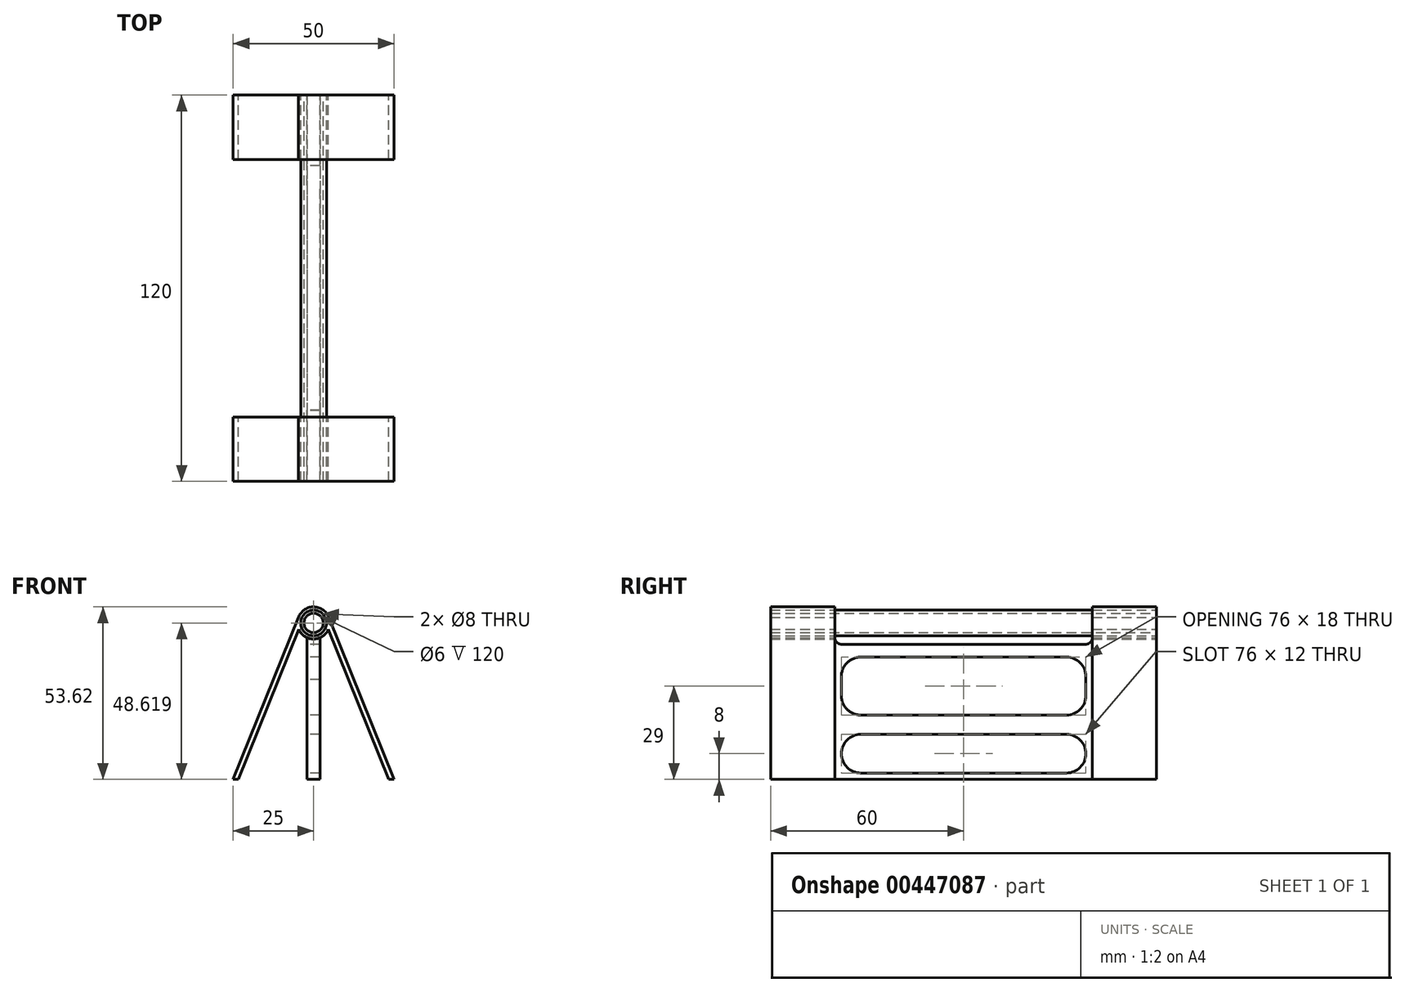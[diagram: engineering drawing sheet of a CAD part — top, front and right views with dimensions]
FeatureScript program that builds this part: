
annotation { "Feature Type Name" : "Feature", "Feature Type Description" : "" }
export const myFeature = defineFeature(function(context is Context, id is Id, definition is map)
    precondition{}
    {
        {
            var Q0;
            Q0=qCreatedBy(makeId("Right.planeOp"),FACE);
            var sketch = newSketch(context, id + "F0", { "sketchPlane" : qUnion([Q0])});
            skLineSegment(sketch, "E0.bottom", {"start": v(0, 48) * mm, "end": v(-120, 48) * mm});
            skLineSegment(sketch, "E0.top", {"start": v(0, 0) * mm, "end": v(-120, 0) * mm});
            skLineSegment(sketch, "E0.left", {"start": v(0, 48) * mm, "end": v(0, 0) * mm});
            skLineSegment(sketch, "E0.right", {"start": v(-120, 48) * mm, "end": v(-120, 0) * mm});
            skArc(sketch, "E1", {"start": v(-92, 32) * mm, "mid": v(-98, 26) * mm, "end": v(-92, 20) * mm});
            skArc(sketch, "E2", {"start": v(-28, 20) * mm, "mid": v(-22, 26) * mm, "end": v(-28, 32) * mm});
            skLineSegment(sketch, "E3", {"start": v(-92, 32) * mm, "end": v(-28, 32) * mm});
            skLineSegment(sketch, "E4", {"start": v(-28, 20) * mm, "end": v(-92, 20) * mm});
            skLineSegment(sketch, "E5", {"start": v(-92, 26) * mm, "end": v(-28, 26) * mm, "construction": true});
            skArc(sketch, "E6", {"start": v(-92, 14) * mm, "mid": v(-98, 8) * mm, "end": v(-92, 2) * mm});
            skArc(sketch, "E7", {"start": v(-28, 2) * mm, "mid": v(-22, 8) * mm, "end": v(-28, 14) * mm});
            skLineSegment(sketch, "E8", {"start": v(-92, 14) * mm, "end": v(-28, 14) * mm});
            skLineSegment(sketch, "E9", {"start": v(-28, 2) * mm, "end": v(-92, 2) * mm});
            skLineSegment(sketch, "E10", {"start": v(-92, 8) * mm, "end": v(-28, 8) * mm, "construction": true});
            skLineSegment(sketch, "E11", {"start": v(-60, 8) * mm, "end": v(-60, 26) * mm, "construction": true});
            skArc(sketch, "E12", {"start": v(-98, 46) * mm, "mid": v(-100, 44) * mm, "end": v(-98, 42) * mm});
            skArc(sketch, "E13", {"start": v(-22, 42) * mm, "mid": v(-20, 44) * mm, "end": v(-22, 46) * mm});
            skLineSegment(sketch, "E14", {"start": v(-98, 46) * mm, "end": v(-22, 46) * mm});
            skLineSegment(sketch, "E15", {"start": v(-22, 42) * mm, "end": v(-98, 42) * mm});
            skLineSegment(sketch, "E16", {"start": v(-98, 44) * mm, "end": v(-22, 44) * mm, "construction": true});
            skArc(sketch, "E17", {"start": v(-92, 38) * mm, "mid": v(-98, 32) * mm, "end": v(-92, 26) * mm});
            skArc(sketch, "E18", {"start": v(-28, 26) * mm, "mid": v(-22, 32) * mm, "end": v(-28, 38) * mm});
            skLineSegment(sketch, "E19", {"start": v(-92, 38) * mm, "end": v(-28, 38) * mm});
            skLineSegment(sketch, "E20", {"start": v(-28, 26) * mm, "end": v(-92, 26) * mm});
            skLineSegment(sketch, "E21", {"start": v(-92, 32) * mm, "end": v(-28, 32) * mm, "construction": true});
            skLineSegment(sketch, "E22", {"start": v(-60, 26) * mm, "end": v(-60, 32) * mm, "construction": true});
            skLineSegment(sketch, "E23", {"start": v(-60, 32) * mm, "end": v(-60, 44) * mm, "construction": true});
            skLineSegment(sketch, "E24", {"start": v(-22, 32) * mm, "end": v(-22, 26) * mm});
            skLineSegment(sketch, "E25", {"start": v(-97.9, 33.12) * mm, "end": v(-98, 26.09) * mm});
            skSolve(sketch);
        }
        {
            var Q0;
            Q0=qCreatedBy(makeId("Front.planeOp"),FACE);
            var sketch = newSketch(context, id + "F1", { "sketchPlane" : qUnion([Q0])});
            skCircle(sketch, "E26", {"center": v(0, 48.62) * mm, "radius": 4 * mm});
            skCircle(sketch, "E27", {"center": v(0, 48.62) * mm, "radius": 5 * mm});
            skLineSegment(sketch, "E28", {"start": v(-25, 0) * mm, "end": v(25, 0) * mm, "construction": true});
            skLineSegment(sketch, "E29", {"start": v(-4.72, 50.28) * mm, "end": v(-25, 0) * mm});
            skLineSegment(sketch, "E30", {"start": v(-4.58, 46.61) * mm, "end": v(-23.38, 0) * mm});
            skLineSegment(sketch, "E31", {"start": v(-13.98, 23.3) * mm, "end": v(-15.37, 23.87) * mm, "construction": true});
            skLineSegment(sketch, "E32", {"start": v(25, 0) * mm, "end": v(4.64, 50.49) * mm});
            skLineSegment(sketch, "E33", {"start": v(4.58, 46.62) * mm, "end": v(23.38, 0) * mm});
            skLineSegment(sketch, "E34", {"start": v(13.49, 24.53) * mm, "end": v(14.88, 25.1) * mm, "construction": true});
            skLineSegment(sketch, "E35", {"start": v(-2, 44.04) * mm, "end": v(-2, 0) * mm});
            skLineSegment(sketch, "E36", {"start": v(-2, 0) * mm, "end": v(2, 0) * mm});
            skLineSegment(sketch, "E37", {"start": v(2, 0) * mm, "end": v(2, 44.04) * mm});
            skLineSegment(sketch, "E38", {"start": v(-25, 0) * mm, "end": v(-23.38, 0) * mm});
            skLineSegment(sketch, "E39", {"start": v(23.38, 0) * mm, "end": v(25, 0) * mm});
            skCircle(sketch, "E40", {"center": v(0, 48.62) * mm, "radius": 3 * mm});
            skSolve(sketch);
        }
        {
            var Q0;
            Q0=makeQuery(id+"F0.imprint","IMPRINT",FACE,{"disambiguationData":[TD([[makeQuery(id+"F0.imprint","IMPRINT",EDGE,{"derivedFrom":sQuery(id+"F0.wireOp",EDGE,"E0.top")}),-1.0]])]});
            extrude(context, id + "F2", {"entities" : qUnion([Q0]), "endBound" : BoundingType.SYMMETRIC, "depth" : 4 * mm});
        }
        {
            var Q0;
            Q0=makeQuery(id+"F1.imprint","IMPRINT",FACE,{"disambiguationData":[TD([[makeQuery(id+"F1.imprint","IMPRINT",EDGE,{"derivedFrom":sQuery(id+"F1.wireOp",EDGE,"E40")}),1.0]])]});
            var Q1;
            Q1=makeQuery(id+"F1.imprint","IMPRINT",FACE,{"disambiguationData":[TD([[makeQuery(id+"F1.imprint","IMPRINT",EDGE,{"derivedFrom":sQuery(id+"F1.wireOp",EDGE,"E26")}),1.0]])]});
            var Q2;
            Q2=makeQuery(id+"F1.imprint","IMPRINT",FACE,{"disambiguationData":[TD([[makeQuery(id+"F1.imprint","IMPRINT",EDGE,{"derivedFrom":sQuery(id+"F1.wireOp",EDGE,"E26")}),-1.0]])]});
            extrude(context, id + "F3", {"entities" : qUnion([Q0, Q1, Q2]), "operationType" : NewBodyOperationType.REMOVE, "depth" : 120 * mm});
        }
        {
            var Q0;
            {var subQ0=sQuery(id+"F1.wireOp",EDGE,"E29");Q0=makeQuery(id+"F1.imprint","IMPRINT",FACE,{"disambiguationData":[TD([[makeQuery(id+"F1.imprint","IMPRINT",EDGE,{"derivedFrom":subQ0}),1.0]])]});}
            var Q1;
            {var subQ0=sQuery(id+"F1.wireOp",EDGE,"E32");Q1=makeQuery(id+"F1.imprint","IMPRINT",FACE,{"disambiguationData":[TD([[makeQuery(id+"F1.imprint","IMPRINT",EDGE,{"derivedFrom":subQ0}),1.0]])]});}
            var Q2;
            Q2=makeQuery(id+"F1.imprint","IMPRINT",FACE,{"disambiguationData":[TD([[makeQuery(id+"F1.imprint","IMPRINT",EDGE,{"derivedFrom":sQuery(id+"F1.wireOp",EDGE,"E26")}),-1.0]])]});
            extrude(context, id + "F4", {"entities" : qUnion([Q0, Q1, Q2]), "depth" : 120 * mm, "hasSecondDirection" : true, "secondDirectionOppositeDirection" : false, "secondDirectionDepth" : 100 * mm});
        }
        {
            var Q0;
            {var subQ0=sQuery(id+"F1.wireOp",EDGE,"E29");Q0=makeQuery(id+"F1.imprint","IMPRINT",FACE,{"disambiguationData":[TD([[makeQuery(id+"F1.imprint","IMPRINT",EDGE,{"derivedFrom":subQ0}),1.0]])]});}
            var Q1;
            {var subQ0=sQuery(id+"F1.wireOp",EDGE,"E32");Q1=makeQuery(id+"F1.imprint","IMPRINT",FACE,{"disambiguationData":[TD([[makeQuery(id+"F1.imprint","IMPRINT",EDGE,{"derivedFrom":subQ0}),1.0]])]});}
            var Q2;
            Q2=makeQuery(id+"F1.imprint","IMPRINT",FACE,{"disambiguationData":[TD([[makeQuery(id+"F1.imprint","IMPRINT",EDGE,{"derivedFrom":sQuery(id+"F1.wireOp",EDGE,"E26")}),-1.0]])]});
            extrude(context, id + "F5", {"entities" : qUnion([Q0, Q1, Q2]), "depth" : 20 * mm});
        }
        {
            var Q0;
            Q0=makeQuery(id+"F1.imprint","IMPRINT",FACE,{"disambiguationData":[TD([[makeQuery(id+"F1.imprint","IMPRINT",EDGE,{"derivedFrom":sQuery(id+"F1.wireOp",EDGE,"E26")}),1.0]])]});
            extrude(context, id + "F6", {"entities" : qUnion([Q0]), "depth" : 120 * mm});
        }
    });
